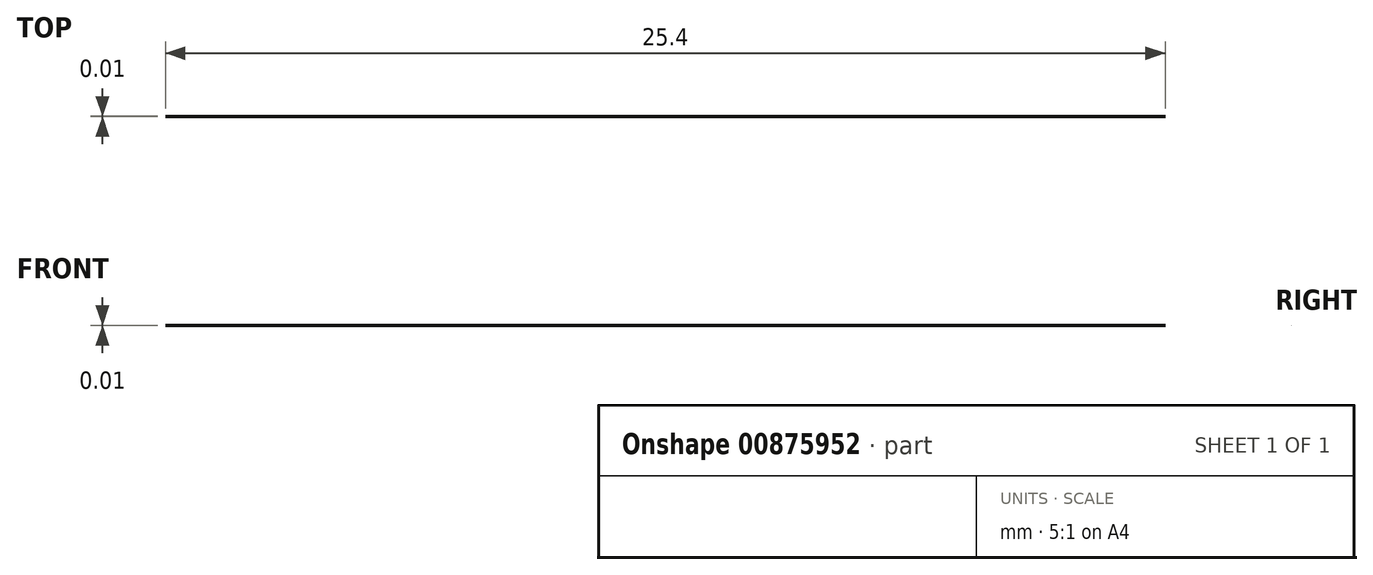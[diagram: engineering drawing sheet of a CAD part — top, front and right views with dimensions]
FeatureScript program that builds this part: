
annotation { "Feature Type Name" : "Feature", "Feature Type Description" : "" }
export const myFeature = defineFeature(function(context is Context, id is Id, definition is map)
    precondition{}
    {
        {
            var Q0;
            Q0=qCreatedBy(makeId("Right.planeOp"),FACE);
            var sketch = newSketch(context, id + "F0", { "sketchPlane" : qUnion([Q0])});
            skLineSegment(sketch, "E0", {"start": v(0, 0) * mm, "end": v(0, 0) * mm});
            skSolve(sketch);
        }
        {
            var Q0;
            Q0=makeQuery(id+"F0.imprint","IMPRINT",FACE,{"disambiguationData":[TD([[makeQuery(id+"F0.imprint","IMPRINT",EDGE,{"derivedFrom":sQuery(id+"F0.wireOp",EDGE,"E0")}),1.0]])]});
            extrude(context, id + "F1", {"entities" : qUnion([Q0]), "depth" : 25.4 * mm, "offsetDistance" : 25.4 * mm});
        }
    });
